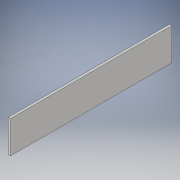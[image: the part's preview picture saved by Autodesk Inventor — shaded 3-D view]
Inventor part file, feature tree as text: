
AUTODESK INVENTOR PART (.ipt)
format: ipt  version: 2017 (Build 210142000, 142)  size: 95,232 bytes
history: native  units: in
note: dims shown in document units (in); Inventor stores cm internally (conversion verified against a paired STEP export)
features: extrude x1, thicken_offset x1, sketch x1
ambient origin geometry x8: Origin, YZ Plane, XZ Plane, XY Plane, X Axis, Y Axis, Z Axis, Center Point
bodies: Solid1 (feature_tree)
feature tree (3):
  extrude  "Extrusion1"  Depth=17.5in
  thicken_offset  "Thicken1"
  sketch  "Sketch1"  dims[d2=3.25in d3=17.5in d4=2.0in d5=1.0in d6=2.0in d7=1.0in d8=0.25in d9=0.0in d10=0.25in d11=0.25in]
